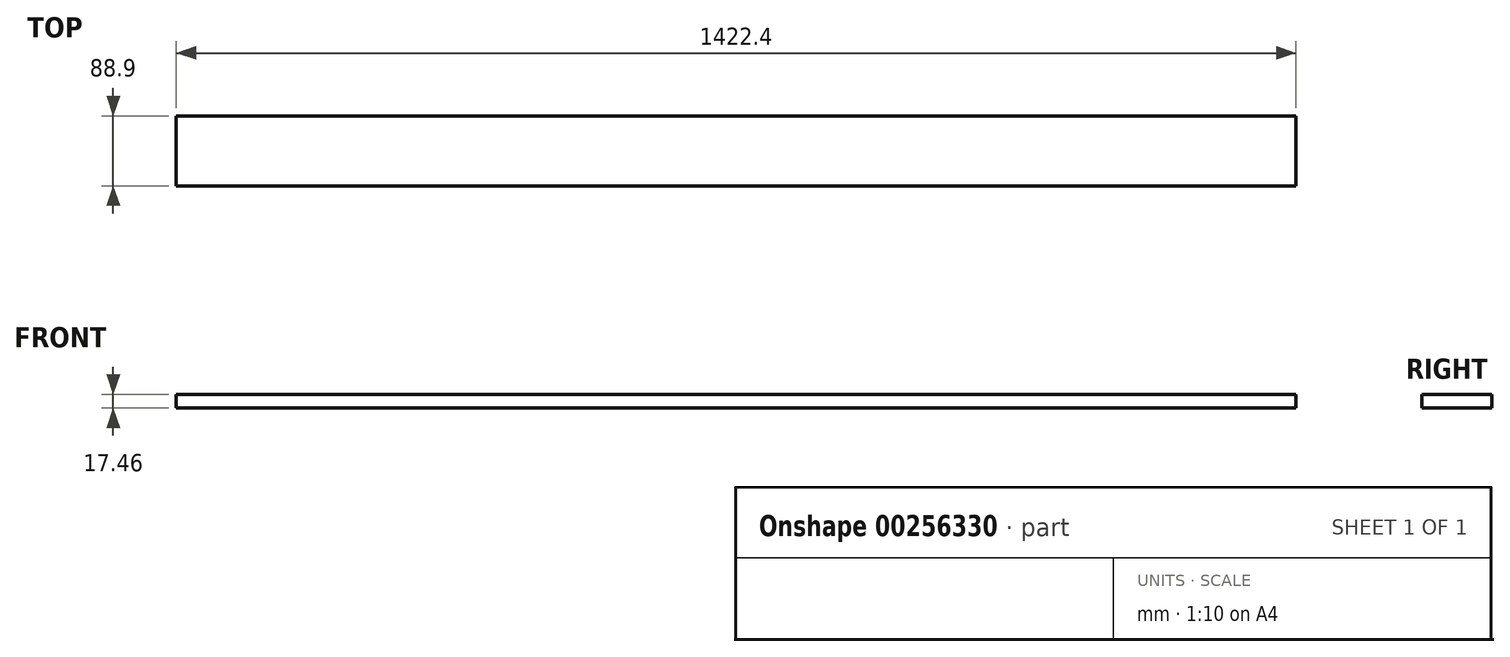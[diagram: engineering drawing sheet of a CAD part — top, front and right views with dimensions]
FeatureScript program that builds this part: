
annotation { "Feature Type Name" : "Feature", "Feature Type Description" : "" }
export const myFeature = defineFeature(function(context is Context, id is Id, definition is map)
    precondition{}
    {
        {
            var Q0;
            Q0=qCreatedBy(makeId("Right.planeOp"),FACE);
            var sketch = newSketch(context, id + "F0", { "sketchPlane" : qUnion([Q0])});
            skLineSegment(sketch, "E0.bottom", {"start": v(-44.45, 8.73) * mm, "end": v(44.45, 8.73) * mm});
            skLineSegment(sketch, "E0.top", {"start": v(-44.45, -8.73) * mm, "end": v(44.45, -8.73) * mm});
            skLineSegment(sketch, "E0.left", {"start": v(-44.45, 8.73) * mm, "end": v(-44.45, -8.73) * mm});
            skLineSegment(sketch, "E0.right", {"start": v(44.45, 8.73) * mm, "end": v(44.45, -8.73) * mm});
            skSolve(sketch);
        }
        {
            var Q0;
            Q0=qSketchRegion(id+"F0",true);
            extrude(context, id + "F1", {"entities" : qUnion([Q0]), "endBound" : BoundingType.SYMMETRIC, "depth" : 1422.4 * mm});
        }
    });
